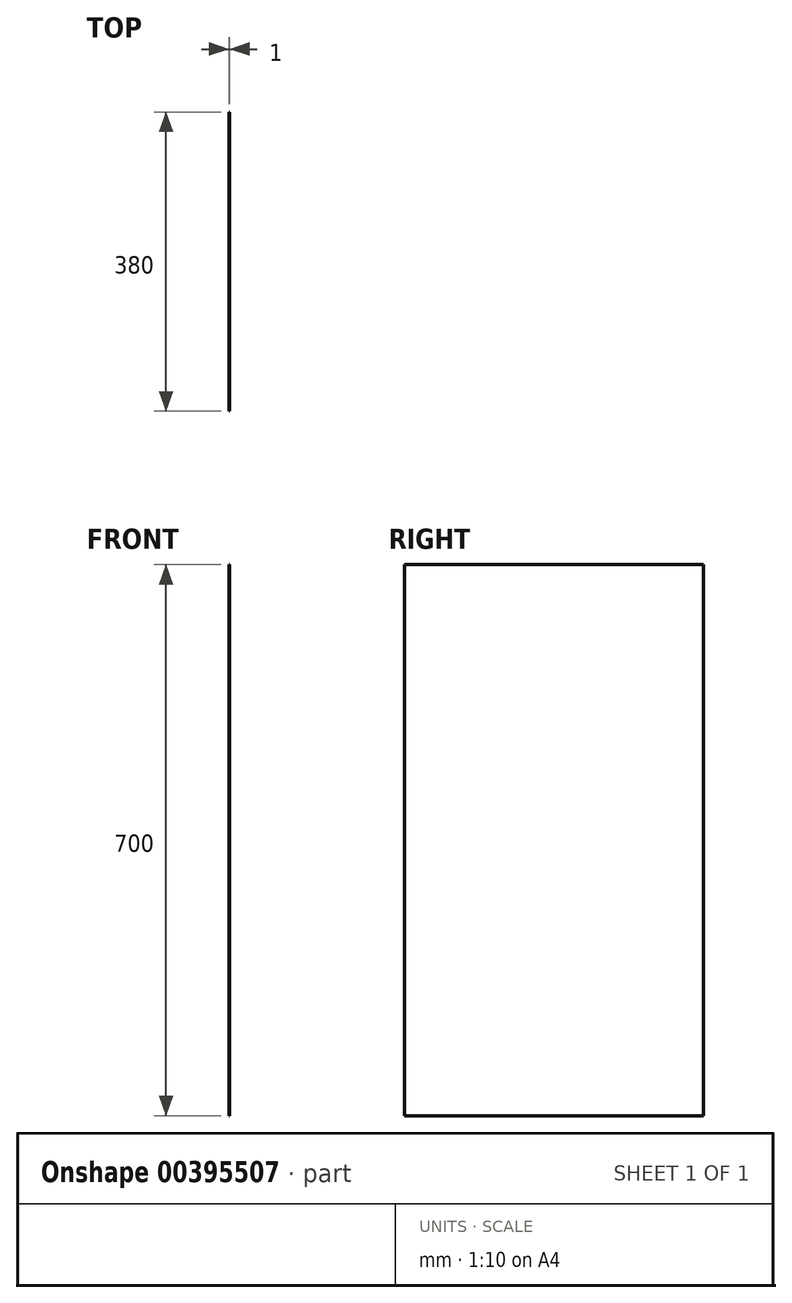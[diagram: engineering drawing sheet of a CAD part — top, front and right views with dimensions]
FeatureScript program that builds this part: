
annotation { "Feature Type Name" : "Feature", "Feature Type Description" : "" }
export const myFeature = defineFeature(function(context is Context, id is Id, definition is map)
    precondition{}
    {
        {
            var Q0;
            Q0=qCreatedBy(makeId("Right.planeOp"),FACE);
            var sketch = newSketch(context, id + "F0", { "sketchPlane" : qUnion([Q0])});
            skLineSegment(sketch, "E0.bottom", {"start": v(190, -350) * mm, "end": v(-190, -350) * mm});
            skLineSegment(sketch, "E0.top", {"start": v(190, 350) * mm, "end": v(-190, 350) * mm});
            skLineSegment(sketch, "E0.left", {"start": v(190, -350) * mm, "end": v(190, 350) * mm});
            skLineSegment(sketch, "E0.right", {"start": v(-190, -350) * mm, "end": v(-190, 350) * mm});
            skPoint(sketch, "E0.middle", {"position": v(0, 0) * mm});
            skSolve(sketch);
        }
        {
            var Q0;
            Q0=makeQuery(id+"F0.imprint","IMPRINT",FACE,{"disambiguationData":[TD([[makeQuery(id+"F0.imprint","IMPRINT",EDGE,{"derivedFrom":sQuery(id+"F0.wireOp",EDGE,"E0.bottom")}),-1.0]])]});
            extrude(context, id + "F1", {"entities" : qUnion([Q0]), "depth" : 1 * mm});
        }
    });
